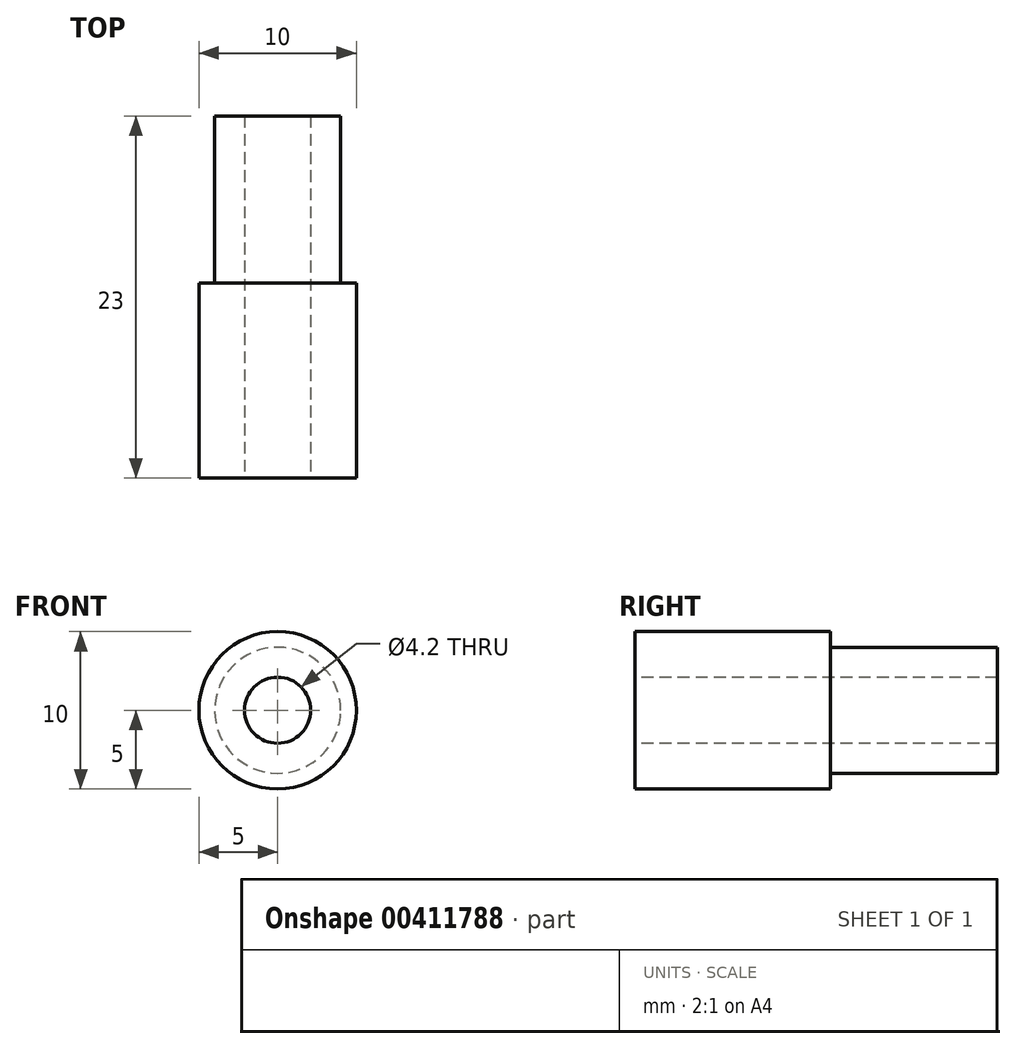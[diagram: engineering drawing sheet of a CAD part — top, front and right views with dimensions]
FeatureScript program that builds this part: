
annotation { "Feature Type Name" : "Feature", "Feature Type Description" : "" }
export const myFeature = defineFeature(function(context is Context, id is Id, definition is map)
    precondition{}
    {
        {
            var Q0;
            Q0=qCreatedBy(makeId("Front.planeOp"),FACE);
            var sketch = newSketch(context, id + "F0", { "sketchPlane" : qUnion([Q0])});
            skCircle(sketch, "E0", {"center": v(0, 0) * mm, "radius": 5 * mm});
            skCircle(sketch, "E1", {"center": v(0, 0) * mm, "radius": 2.1 * mm});
            skSolve(sketch);
        }
        {
            var Q0;
            Q0=qSketchRegion(id+"F0",true);
            extrude(context, id + "F1", {"entities" : qUnion([Q0]), "oppositeDirection" : true, "depth" : 12.4 * mm});
        }
        {
            var Q0;
            Q0=makeQuery(id+"F1.opExtrude","CAP_FACE",FACE,{"disambiguationData":[OSD([sQuery(id+"F0.wireOp",EDGE,"E0"),sQuery(id+"F0.wireOp",EDGE,"E1")])],"isStart":false});
            var sketch = newSketch(context, id + "F2", { "sketchPlane" : qUnion([Q0])});
            skCircle(sketch, "E2", {"center": v(0, 0) * mm, "radius": 4 * mm});
            skSolve(sketch);
        }
        {
            var Q0;
            Q0=makeQuery(id+"F2.imprint","IMPRINT",FACE,{"disambiguationData":[TD([[makeQuery(id+"F2.imprint","IMPRINT",EDGE,{"derivedFrom":sQuery(id+"F2.wireOp",EDGE,"E2")}),1.0]])]});
            extrude(context, id + "F3", {"entities" : qUnion([Q0]), "operationType" : NewBodyOperationType.ADD, "depth" : 10.6 * mm});
        }
    });
